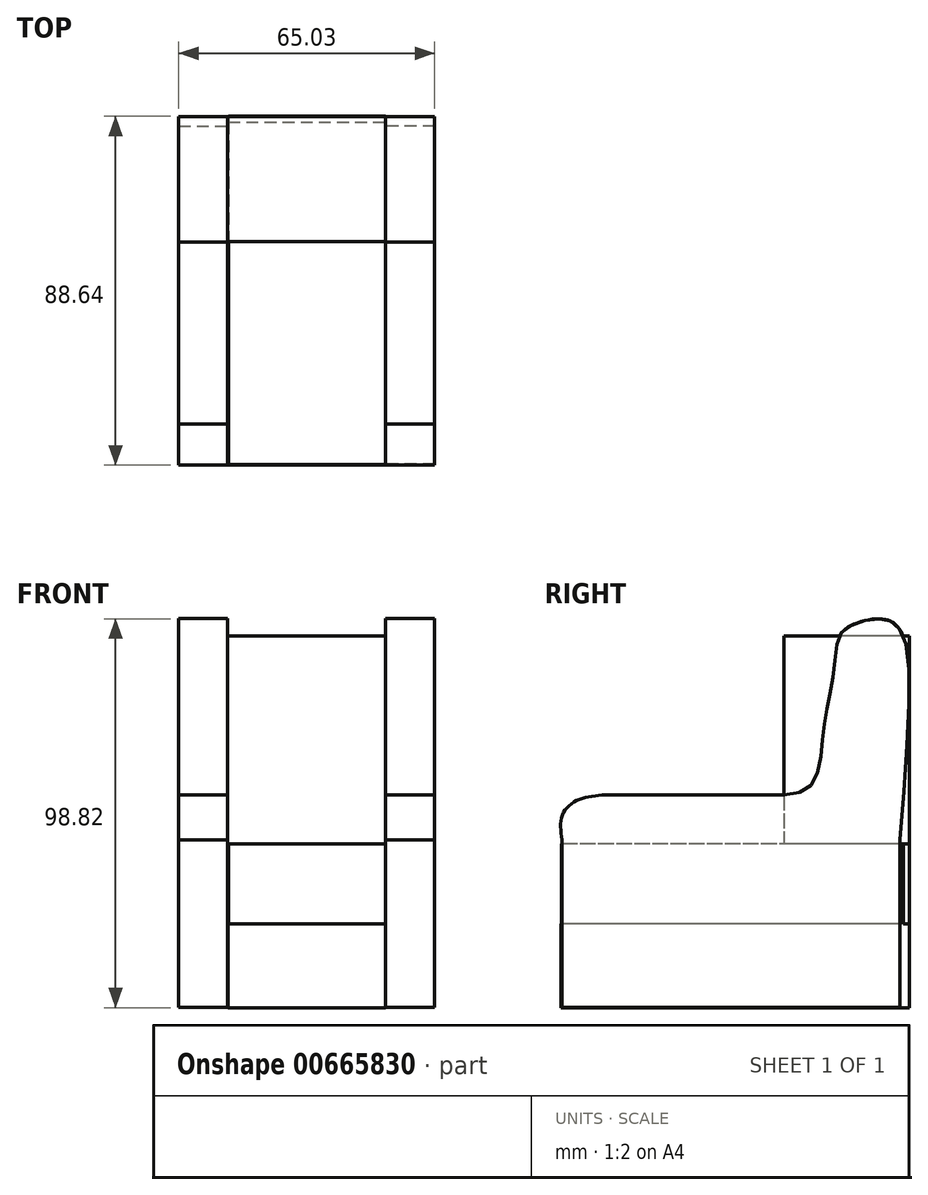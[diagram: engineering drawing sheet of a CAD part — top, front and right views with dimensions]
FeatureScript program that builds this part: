
annotation { "Feature Type Name" : "Feature", "Feature Type Description" : "" }
export const myFeature = defineFeature(function(context is Context, id is Id, definition is map)
    precondition{}
    {
        {
            var Q0;
            Q0=qCreatedBy(makeId("Right.planeOp"),FACE);
            var sketch = newSketch(context, id + "F0", { "sketchPlane" : qUnion([Q0])});
            skLineSegment(sketch, "E0.bottom", {"start": v(-42.9, 21.3) * mm, "end": v(42.9, 21.3) * mm});
            skLineSegment(sketch, "E0.top", {"start": v(-42.9, -21.3) * mm, "end": v(42.9, -21.3) * mm});
            skLineSegment(sketch, "E0.left", {"start": v(-42.9, 21.3) * mm, "end": v(-42.9, -21.3) * mm});
            skLineSegment(sketch, "E0.right", {"start": v(42.9, 21.3) * mm, "end": v(42.9, -21.3) * mm});
            skPoint(sketch, "E0.middle", {"position": v(0, 0) * mm});
            skFitSpline(sketch, "E1", {"points": [v(-42.9, 21.3) * mm, v(-42.9, 27.38) * mm, v(-39.24, 31.23) * mm, v(-32.75, 32.65) * mm], "startDerivative": vector(-2.75, 19.2) * mm, "endDerivative": vector(19.64, 2.13) * mm});
            skLineSegment(sketch, "E2", {"start": v(-32.75, 32.65) * mm, "end": v(13.49, 32.65) * mm});
            skFitSpline(sketch, "E3", {"points": [v(13.49, 32.65) * mm, v(19.98, 34.68) * mm, v(22.61, 40.97) * mm, v(23.63, 49.69) * mm, v(24.84, 56.79) * mm, v(26.26, 65.5) * mm, v(27.48, 72.81) * mm, v(30.73, 75.85) * mm, v(37.22, 77.47) * mm, v(41.27, 76.46) * mm, v(44.52, 70.58) * mm, v(42.9, 21.3) * mm], "startDerivative": vector(93.37, 12.7) * mm, "endDerivative": vector(-24.12, -284.75) * mm});
            skSolve(sketch);
        }
        {
            var Q0;
            Q0 = qSketchRegion(id + "F0", true);
            extrude(context, id + "F1", {"entities" : qUnion([Q0]), "depth" : 12.45 * mm, "offsetDistance" : 25.4 * mm});
        }
        {
            var Q0;
            Q0=qCreatedBy(makeId("Right.planeOp"),FACE);
            cPlane(context, id + "F2", {"entities" : qUnion([Q0]), "cplaneType" : CPlaneType.OFFSET, "offset" : 20.07 * mm, "oppositeDirection" : true, "width" : 152.4 * mm, "height" : 152.4 * mm});
        }
        {
            var Q0;
            Q0=makeQuery(id+"F1.opExtrude","SWEPT_BODY",BODY,{"disambiguationData":[OSD([sQuery(id+"F0.wireOp",EDGE,"E0.top"),sQuery(id+"F0.wireOp",EDGE,"E0.left"),sQuery(id+"F0.wireOp",EDGE,"E0.right"),sQuery(id+"F0.wireOp",EDGE,"E1"),sQuery(id+"F0.wireOp",EDGE,"E2"),sQuery(id+"F0.wireOp",EDGE,"E3")])]});
            var Q1;
            Q1=qCreatedBy(id+"F2.planeOp",FACE);
            mirror(context, id + "F3", {"entities" : qUnion([Q0]), "mirrorPlane" : qUnion([Q1])});
        }
        {
            var Q0;
            Q0=qCreatedBy(makeId("Top.planeOp"),FACE);
            var sketch = newSketch(context, id + "F4", { "sketchPlane" : qUnion([Q0])});
            skLineSegment(sketch, "E4.bottom", {"start": v(0, 45.35) * mm, "end": v(-40.1, 45.35) * mm});
            skLineSegment(sketch, "E4.top", {"start": v(0, -43.18) * mm, "end": v(-40.1, -43.18) * mm});
            skLineSegment(sketch, "E4.left", {"start": v(0, 45.35) * mm, "end": v(0, -43.18) * mm});
            skLineSegment(sketch, "E4.right", {"start": v(-40.1, 45.35) * mm, "end": v(-40.1, -43.18) * mm});
            skSolve(sketch);
        }
        {
            var Q0;
            Q0 = qSketchRegion(id + "F4", true);
            extrude(context, id + "F5", {"entities" : qUnion([Q0]), "operationType" : NewBodyOperationType.ADD, "oppositeDirection" : true, "depth" : 21.34 * mm, "offsetDistance" : 25.4 * mm});
        }
        {
            var Q0;
            Q0=qCreatedBy(makeId("Top.planeOp"),FACE);
            var sketch = newSketch(context, id + "F6", { "sketchPlane" : qUnion([Q0])});
            skLineSegment(sketch, "E5.bottom", {"start": v(-39.96, 43.87) * mm, "end": v(0, 43.87) * mm});
            skLineSegment(sketch, "E5.top", {"start": v(-39.96, -43.04) * mm, "end": v(0, -43.04) * mm});
            skLineSegment(sketch, "E5.left", {"start": v(-39.96, 43.87) * mm, "end": v(-39.96, -43.04) * mm});
            skLineSegment(sketch, "E5.right", {"start": v(0, 43.87) * mm, "end": v(0, -43.04) * mm});
            skSolve(sketch);
        }
        {
            var Q0;
            Q0 = qSketchRegion(id + "F6", true);
            extrude(context, id + "F7", {"entities" : qUnion([Q0]), "operationType" : NewBodyOperationType.ADD, "depth" : 20.32 * mm, "offsetDistance" : 25.4 * mm});
        }
        {
            var Q0;
            Q0=makeQuery(id+"F7.opExtrude","CAP_FACE",FACE,{"disambiguationData":[OSD([sQuery(id+"F6.wireOp",EDGE,"E5.bottom"),sQuery(id+"F6.wireOp",EDGE,"E5.top"),sQuery(id+"F6.wireOp",EDGE,"E5.left"),sQuery(id+"F6.wireOp",EDGE,"E5.right")])],"isStart":false});
            var sketch = newSketch(context, id + "F8", { "sketchPlane" : qUnion([Q0])});
            skLineSegment(sketch, "E6.bottom", {"start": v(-40.16, 45.31) * mm, "end": v(0, 45.31) * mm});
            skLineSegment(sketch, "E6.top", {"start": v(-40.16, 13.55) * mm, "end": v(0, 13.55) * mm});
            skLineSegment(sketch, "E6.left", {"start": v(-40.16, 45.31) * mm, "end": v(-40.16, 13.55) * mm});
            skLineSegment(sketch, "E6.right", {"start": v(0, 45.31) * mm, "end": v(0, 13.55) * mm});
            skSolve(sketch);
        }
        {
            var Q0;
            Q0 = qSketchRegion(id + "F8", true);
            extrude(context, id + "F9", {"entities" : qUnion([Q0]), "depth" : 52.83 * mm, "offsetDistance" : 25.4 * mm});
        }
        {
            var Q0;
            Q0=makeQuery(id+"F7.opExtrude","SWEPT_FACE",FACE,{"disambiguationData":[OSD([sQuery(id+"F6.wireOp",EDGE,"E5.bottom")])]});
            var sketch = newSketch(context, id + "F10", { "sketchPlane" : qUnion([Q0])});
            skLineSegment(sketch, "E7.bottom", {"start": v(0, 20.32) * mm, "end": v(39.96, 20.32) * mm});
            skLineSegment(sketch, "E7.top", {"start": v(0, 0) * mm, "end": v(39.96, 0) * mm});
            skLineSegment(sketch, "E7.left", {"start": v(0, 20.32) * mm, "end": v(0, 0) * mm});
            skLineSegment(sketch, "E7.right", {"start": v(39.96, 20.32) * mm, "end": v(39.96, 0) * mm});
            skSolve(sketch);
        }
        {
            var Q0;
            Q0 = qSketchRegion(id + "F10", true);
            extrude(context, id + "F11", {"entities" : qUnion([Q0]), "depth" : 1.52 * mm, "offsetDistance" : 25.4 * mm});
        }
    });
